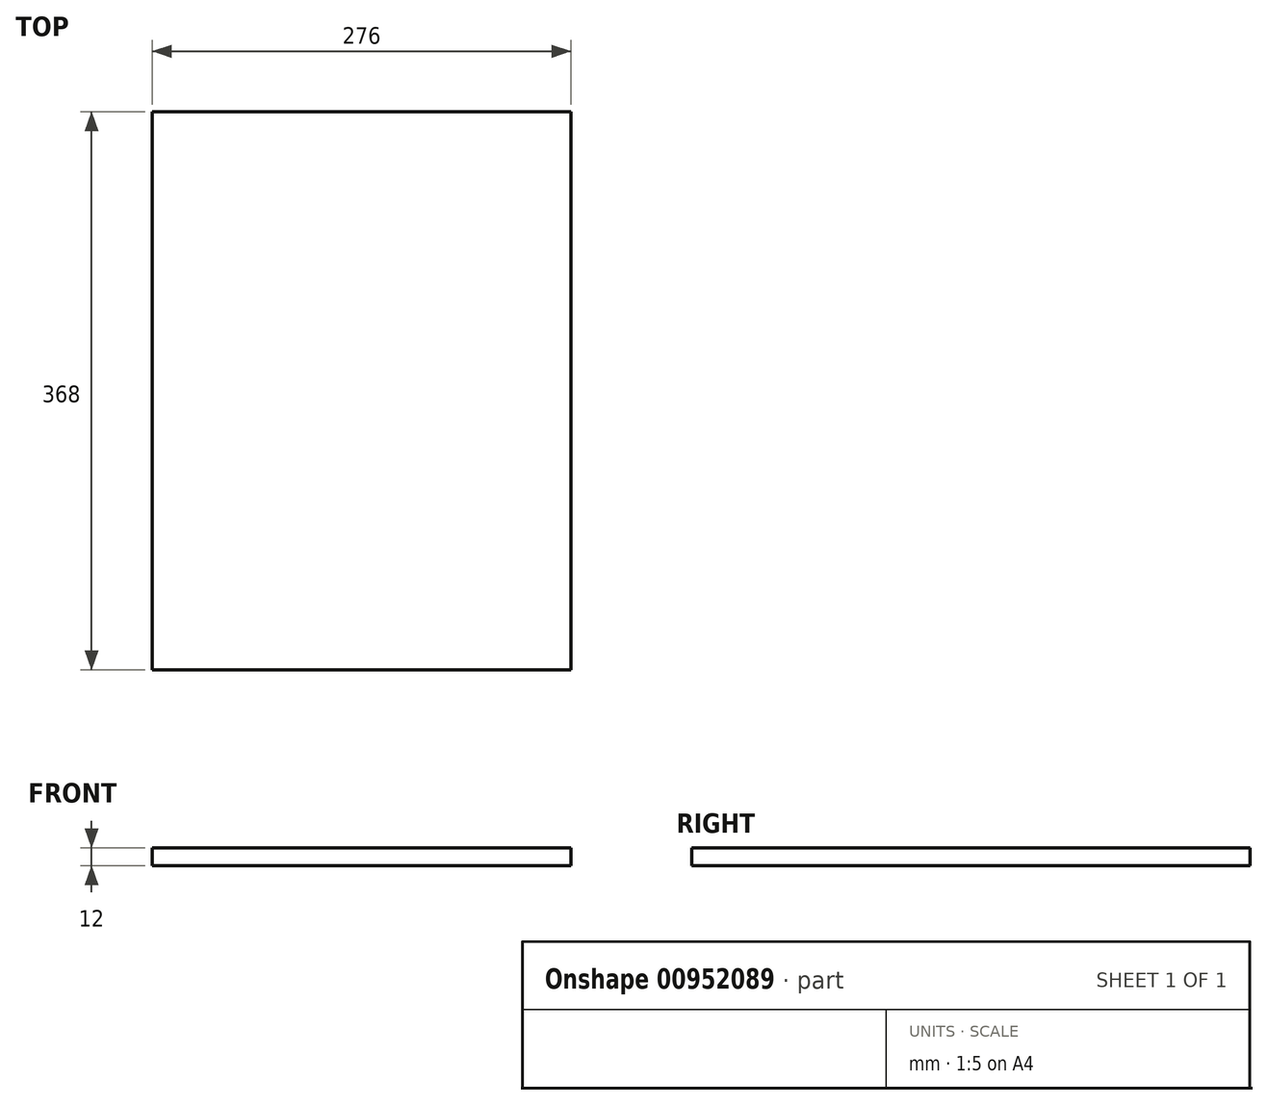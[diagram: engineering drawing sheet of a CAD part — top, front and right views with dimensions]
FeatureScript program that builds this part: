
annotation { "Feature Type Name" : "Feature", "Feature Type Description" : "" }
export const myFeature = defineFeature(function(context is Context, id is Id, definition is map)
    precondition{}
    {
        {
            var Q0;
            Q0=qCreatedBy(makeId("Top.planeOp"),FACE);
            var sketch = newSketch(context, id + "F0", { "sketchPlane" : qUnion([Q0])});
            skLineSegment(sketch, "E0.bottom", {"start": v(138, -184) * mm, "end": v(-138, -184) * mm});
            skLineSegment(sketch, "E0.top", {"start": v(138, 184) * mm, "end": v(-138, 184) * mm});
            skLineSegment(sketch, "E0.left", {"start": v(138, -184) * mm, "end": v(138, 184) * mm});
            skLineSegment(sketch, "E0.right", {"start": v(-138, -184) * mm, "end": v(-138, 184) * mm});
            skPoint(sketch, "E0.middle", {"position": v(0, 0) * mm});
            skSolve(sketch);
        }
        {
            var Q0;
            Q0=makeQuery(id+"F0.imprint","IMPRINT",FACE,{"disambiguationData":[TD([[makeQuery(id+"F0.imprint","IMPRINT",EDGE,{"derivedFrom":sQuery(id+"F0.wireOp",EDGE,"E0.bottom")}),-1.0]])]});
            extrude(context, id + "F1", {"entities" : qUnion([Q0]), "depth" : 12 * mm, "offsetDistance" : 25 * mm});
        }
    });
